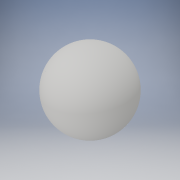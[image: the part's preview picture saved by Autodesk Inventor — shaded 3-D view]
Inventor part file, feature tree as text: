
AUTODESK INVENTOR PART (.ipt)
format: ipt  version: 2018 (Build 220112000, 112)  size: 129,024 bytes
history: native  units: in
note: dims shown in document units (in); Inventor stores cm internally (conversion verified against a paired STEP export)
features: revolve x1, sketch x1
ambient origin geometry x8: Origin, YZ Plane, XZ Plane, XY Plane, X Axis, Y Axis, Z Axis, Center Point
bodies: Solid1 (feature_tree)
feature tree (2):
  revolve  "Revolution1"  [1 undecoded]
  sketch  "Sketch1"  dims[d0=19.685in d1=0.0in d2=90.0deg]
note: 1 required parameter value undecoded (feature->parameter linkage not recoverable at this tier; creation-order binding heuristic only, values carry confidence <= 0.55)
